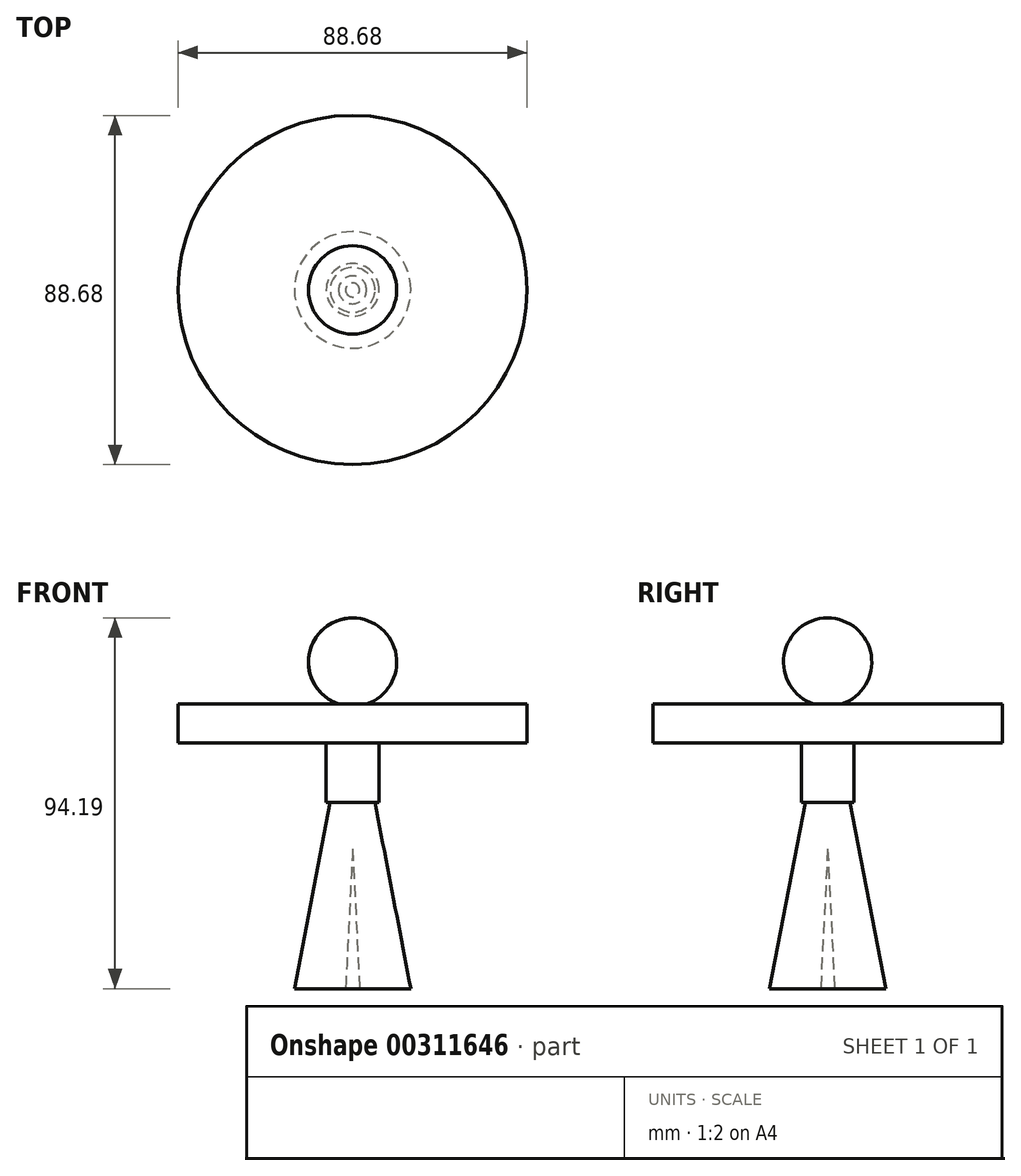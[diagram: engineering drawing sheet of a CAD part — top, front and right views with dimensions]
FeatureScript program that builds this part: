
annotation { "Feature Type Name" : "Feature", "Feature Type Description" : "" }
export const myFeature = defineFeature(function(context is Context, id is Id, definition is map)
    precondition{}
    {
        {
            var Q0;
            Q0=qCreatedBy(makeId("Front.planeOp"),FACE);
            var sketch = newSketch(context, id + "F0", { "sketchPlane" : qUnion([Q0])});
            skLineSegment(sketch, "E0.0", {"start": v(0, 55.38) * mm, "end": v(-5.69, 55.38) * mm});
            skPoint(sketch, "E0.0.midPoint", {"position": v(0, 55.38) * mm});
            skLineSegment(sketch, "E1.bottom", {"start": v(-5.69, 55.38) * mm, "end": v(0, 55.38) * mm});
            skLineSegment(sketch, "E1.top", {"start": v(-5.69, 30.35) * mm, "end": v(0, 30.35) * mm});
            skLineSegment(sketch, "E2", {"start": v(-5.69, 30.35) * mm, "end": v(-14.78, -16.95) * mm});
            skLineSegment(sketch, "E3", {"start": v(-14.78, -16.95) * mm, "end": v(-1.77, -16.95) * mm});
            skLineSegment(sketch, "E4", {"start": v(-1.77, -16.95) * mm, "end": v(0, 18.52) * mm});
            skArc(sketch, "E5", {"start": v(0, 77.24) * mm, "mid": v(-11.22, 66.02) * mm, "end": v(0, 54.8) * mm});
            skLineSegment(sketch, "E6", {"start": v(-6.7, 45.52) * mm, "end": v(-6.7, 30.35) * mm});
            skLineSegment(sketch, "E7", {"start": v(-6.7, 30.35) * mm, "end": v(-6.7, 45.52) * mm});
            skLineSegment(sketch, "E8", {"start": v(-44.34, 45.52) * mm, "end": v(-6.7, 45.52) * mm});
            skLineSegment(sketch, "E9", {"start": v(-44.34, 45.52) * mm, "end": v(-44.34, 55.38) * mm});
            skLineSegment(sketch, "E10", {"start": v(-44.34, 55.38) * mm, "end": v(-5.69, 55.38) * mm});
            skLineSegment(sketch, "E11", {"start": v(-6.7, 30.35) * mm, "end": v(-5.69, 30.35) * mm});
            skLineSegment(sketch, "E12", {"start": v(0, 55.38) * mm, "end": v(0, 30.35) * mm});
            skLineSegment(sketch, "E13", {"start": v(0, 77.24) * mm, "end": v(0, 18.52) * mm});
            skPoint(sketch, "E14.trimOffspring.end.orphan", {"position": v(5.91, 55.38) * mm});
            skPoint(sketch, "E14.trimOffspring.start.orphan", {"position": v(5.69, 55.38) * mm});
            skPoint(sketch, "E15.end.orphan", {"position": v(40.4, 45.52) * mm});
            skPoint(sketch, "E16.start.orphan", {"position": v(5.91, 45.52) * mm});
            skSolve(sketch);
        }
        {
            var Q0;
            Q0 = qSketchRegion(id + "F0", true);
            var Q1;
            Q1=sQuery(id+"F0.wireOp",EDGE,"E13");
            revolve(context, id + "F1", {"entities" : qUnion([Q0]), "axis" : qUnion([Q1]), "revolveType" : RevolveType.FULL});
        }
    });
